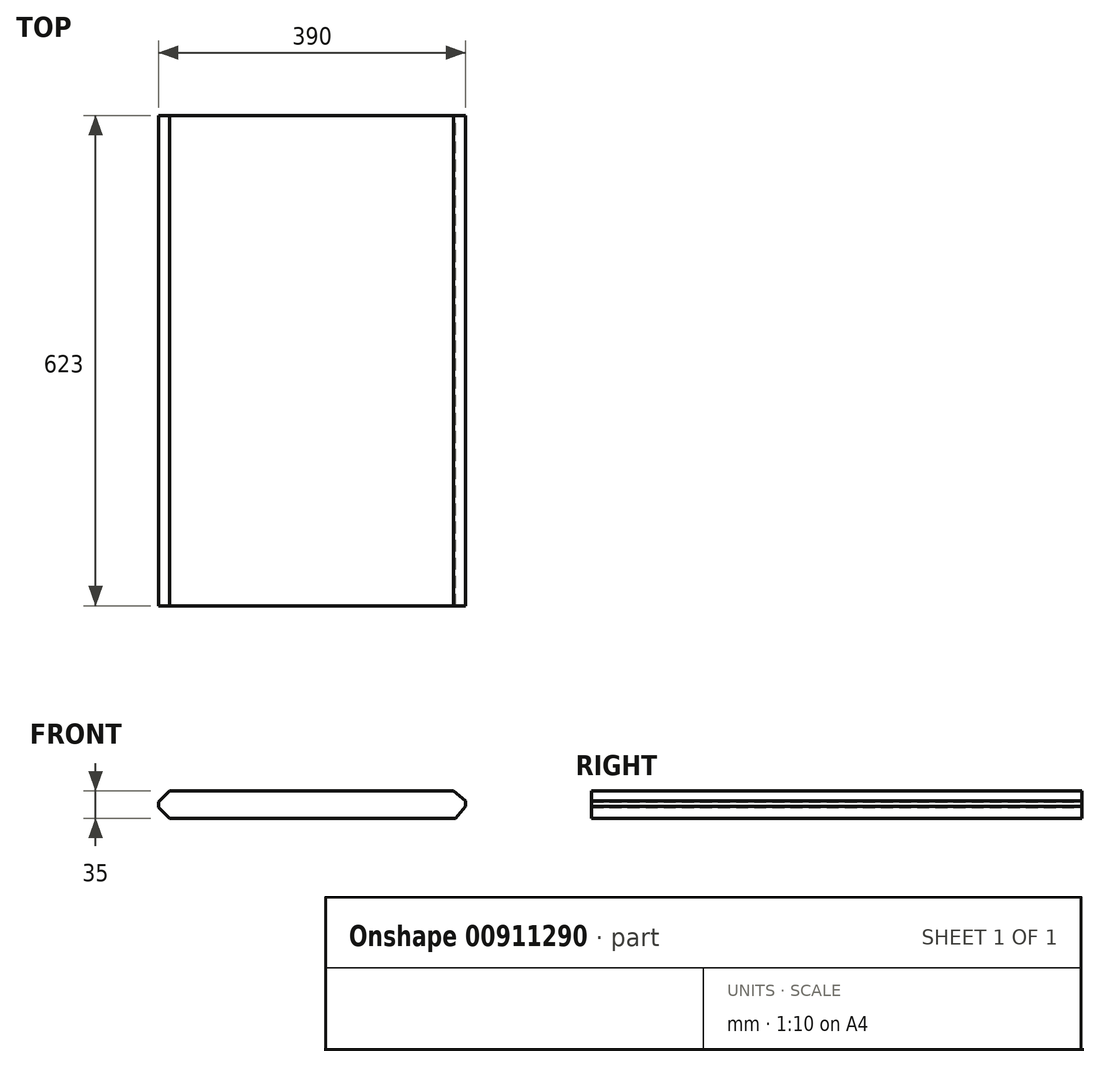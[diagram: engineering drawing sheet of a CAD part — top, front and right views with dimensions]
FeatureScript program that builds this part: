
annotation { "Feature Type Name" : "Feature", "Feature Type Description" : "" }
export const myFeature = defineFeature(function(context is Context, id is Id, definition is map)
    precondition{}
    {
        {
            var Q0;
            Q0=qCreatedBy(makeId("Front.planeOp"),FACE);
            var sketch = newSketch(context, id + "F0", { "sketchPlane" : qUnion([Q0])});
            skLineSegment(sketch, "E0.bottom", {"start": v(-199.14, 16.91) * mm, "end": v(161.84, 16.91) * mm});
            skLineSegment(sketch, "E0.top", {"start": v(-199.14, -18.09) * mm, "end": v(164.07, -18.09) * mm});
            skLineSegment(sketch, "E0.left", {"start": v(-213.14, 2.91) * mm, "end": v(-213.14, -4.09) * mm});
            skLineSegment(sketch, "E0.right", {"start": v(176.86, 4.02) * mm, "end": v(176.86, -2.98) * mm});
            skLineSegment(sketch, "E1", {"start": v(-199.14, 16.91) * mm, "end": v(-213.14, 2.91) * mm});
            skLineSegment(sketch, "E2", {"start": v(-213.14, -4.09) * mm, "end": v(-199.14, -18.09) * mm});
            skLineSegment(sketch, "E3", {"start": v(164.07, -18.09) * mm, "end": v(176.86, -2.98) * mm});
            skLineSegment(sketch, "E4", {"start": v(176.86, -2.98) * mm, "end": v(176.86, 4.02) * mm});
            skLineSegment(sketch, "E5", {"start": v(176.86, 4.02) * mm, "end": v(161.84, 16.91) * mm});
            skLineSegment(sketch, "E6", {"start": v(161.84, 16.91) * mm, "end": v(-199.14, 16.91) * mm});
            skPoint(sketch, "E7.orphan", {"position": v(-213.14, 16.91) * mm});
            skSolve(sketch);
        }
        {
            var Q0;
            Q0 = qSketchRegion(id + "F0", true);
            extrude(context, id + "F1", {"entities" : qUnion([Q0]), "depth" : 311.5 * mm, "offsetDistance" : 25.4 * mm, "hasSecondDirection" : true, "secondDirectionOppositeDirection" : true, "secondDirectionDepth" : 311.5 * mm});
        }
    });
